FCSTD DOCUMENT  (FreeCAD 0.17R13541 (Git))
Label: Xtrusion4mmx4.5
License: All rights reserved
LicenseURL: http://en.wikipedia.org/wiki/All_rights_reserved
objects: Sketcher::SketchObject×1
note: 1 computed .brp shape members not serialized (recipe doc carries the construction recipe); baked Part::Feature solids carry a one-line shape summary decoded from their .brp

FEATURE [Sketcher::SketchObject] Sketch
  sketch-geometry (28):
    g0: LineSegment StartX=-73.7749 StartY=-24.5454 StartZ=0 EndX=-61.2522 EndY=-24.5454 EndZ=0
    g1: LineSegment StartX=-61.2522 StartY=-24.5454 StartZ=0 EndX=-65.7522 EndY=-20.0454 EndZ=0
    g2: LineSegment StartX=-65.7522 StartY=-20.0454 StartZ=0 EndX=-52.7522 EndY=-20.0454 EndZ=0
    g3: LineSegment StartX=-52.7522 StartY=-20.0454 StartZ=0 EndX=-57.2522 EndY=-24.5454 EndZ=0
    g4: LineSegment StartX=-57.2522 StartY=-24.5454 StartZ=0 EndX=-44.7295 EndY=-24.5454 EndZ=0
    g5: LineSegment StartX=-44.7295 StartY=-24.5454 StartZ=0 EndX=-44.7295 EndY=-12.0227 EndZ=0
    g6: LineSegment StartX=-44.7295 StartY=-12.0227 StartZ=0 EndX=-49.2295 EndY=-16.5227 EndZ=0
    g7: LineSegment StartX=-49.2295 StartY=-16.5227 StartZ=0 EndX=-49.2295 EndY=-3.52271 EndZ=0
    g8: LineSegment StartX=-49.2295 StartY=-3.52271 StartZ=0 EndX=-44.7295 EndY=-8.02271 EndZ=0
    g9: LineSegment StartX=-44.7295 StartY=-8.02271 StartZ=0 EndX=-44.7295 EndY=4.5 EndZ=0
    g10: LineSegment StartX=-44.7295 StartY=4.5 StartZ=0 EndX=-57.2522 EndY=4.5 EndZ=0
    g11: LineSegment StartX=-57.2522 StartY=4.5 StartZ=0 EndX=-52.7522 EndY=0 EndZ=0
    g12: LineSegment StartX=-52.7522 StartY=0 StartZ=0 EndX=-65.7522 EndY=0 EndZ=0
    g13: LineSegment StartX=-65.7522 StartY=0 StartZ=0 EndX=-61.2522 EndY=4.5 EndZ=0
    g14: LineSegment StartX=-61.2522 StartY=4.5 StartZ=0 EndX=-73.7749 EndY=4.5 EndZ=0
    g15: LineSegment StartX=-73.7749 StartY=4.5 StartZ=0 EndX=-73.7749 EndY=-8.02271 EndZ=0
    g16: LineSegment StartX=-73.7749 StartY=-8.02271 StartZ=0 EndX=-69.2749 EndY=-3.52271 EndZ=0
    g17: LineSegment StartX=-69.2749 StartY=-3.52271 StartZ=0 EndX=-69.2749 EndY=-16.5227 EndZ=0
    g18: LineSegment StartX=-69.2749 StartY=-16.5227 StartZ=0 EndX=-73.7749 EndY=-12.0227 EndZ=0
    g19: LineSegment StartX=-73.7749 StartY=-12.0227 StartZ=0 EndX=-73.7749 EndY=-24.5454 EndZ=0
    g20: LineSegment [constr] StartX=-61.2522 StartY=-24.5454 StartZ=0 EndX=-57.2522 EndY=-24.5454 EndZ=0
    g21: LineSegment [constr] StartX=-61.2522 StartY=4.5 StartZ=0 EndX=-57.2522 EndY=4.5 EndZ=0
    g22: LineSegment [constr] StartX=-44.7295 StartY=-8.02271 StartZ=0 EndX=-44.7295 EndY=-12.0227 EndZ=0
    g23: LineSegment [constr] StartX=-73.7749 StartY=-8.02271 StartZ=0 EndX=-73.7749 EndY=-12.0227 EndZ=0
    g24: LineSegment [constr] StartX=-65.7522 StartY=-20.0454 StartZ=0 EndX=-65.7522 EndY=-24.5454 EndZ=0
    g25: LineSegment [constr] StartX=-69.2749 StartY=-16.5227 StartZ=0 EndX=-73.7749 EndY=-16.5227 EndZ=0
    g26: LineSegment [constr] StartX=-65.7522 StartY=4.5 StartZ=0 EndX=-65.7522 EndY=0 EndZ=0
    g27: LineSegment [constr] StartX=-49.2295 StartY=-3.52271 StartZ=0 EndX=-44.7295 EndY=-3.52271 EndZ=0
  constraints (82):
    c: Horizontal(g0)
    c: Coincident(g0,g1)
    c: Coincident(g1,g2)
    c: Horizontal(g2)
    c: Coincident(g2,g3)
    c: Coincident(g3,g4)
    c: Horizontal(g4)
    c: Coincident(g4,g5)
    c: Vertical(g5)
    c: Coincident(g5,g6)
    c: Coincident(g6,g7)
    c: Vertical(g7)
    c: Coincident(g7,g8)
    c: Coincident(g8,g9)
    c: Vertical(g9)
    c: Coincident(g9,g10)
    c: Horizontal(g10)
    c: Coincident(g10,g11)
    c: Coincident(g11,g12)
    c: PointOnObject(g12,g-1)
    c: Horizontal(g12)
    c: Coincident(g12,g13)
    c: Coincident(g13,g14)
    c: Horizontal(g14)
    c: Coincident(g14,g15)
    c: Vertical(g15)
    c: Coincident(g15,g16)
    c: Coincident(g16,g17)
    c: Vertical(g17)
    c: Coincident(g17,g18)
    c: Coincident(g18,g19)
    c: Vertical(g19)
    c: Equal(g14,g10)
    c: Equal(g10,g9)
    c: Equal(g9,g5)
    c: Equal(g5,g4)
    c: Equal(g4,g0)
    c: Equal(g0,g19)
    c: Equal(g19,g15)
    c: Equal(g17,g12)
    c: Equal(g12,g7)
    c: Equal(g7,g2)
    c: Angle(g1,g0) = 0.785398
    c: Angle(g19,g18) = 0.785398
    c: Angle(g4,g3) = 0.785398
    c: Angle(g6,g5) = 0.785398
    c: Angle(g9,g8) = 0.785398
    c: Angle(g11,g10) = 0.785398
    c: Angle(g14,g13) = 0.785398
    c: Angle(g16,g15) = 0.785398
    c: Equal(g16,g13)
    c: Equal(g13,g11)
    c: Equal(g11,g8)
    c: Equal(g8,g6)
    c: Equal(g6,g3)
    c: Equal(g3,g1)
    c: Equal(g1,g18)
    c: Coincident(g20,g0)
    c: Coincident(g20,g3)
    c: Coincident(g21,g13)
    c: Coincident(g21,g10)
    c: Coincident(g22,g8)
    c: Coincident(g22,g5)
    c: Coincident(g23,g15)
    c: Coincident(g23,g18)
    c: Equal(g23,g21)
    c: Equal(g21,g22)
    c: Equal(g22,g20)
    c: Distance(g21) = 4
    c: Coincident(g24,g1)
    c: PointOnObject(g24,g0)
    c: Vertical(g24)
    c: Coincident(g25,g17)
    c: PointOnObject(g25,g19)
    c: Horizontal(g25)
    c: PointOnObject(g26,g14)
    c: Coincident(g26,g12)
    c: Coincident(g27,g7)
    c: Horizontal(g27)
    c: Equal(g27,g26)
    c: Equal(g26,g25)
    c: Distance(g26) = 4.5
